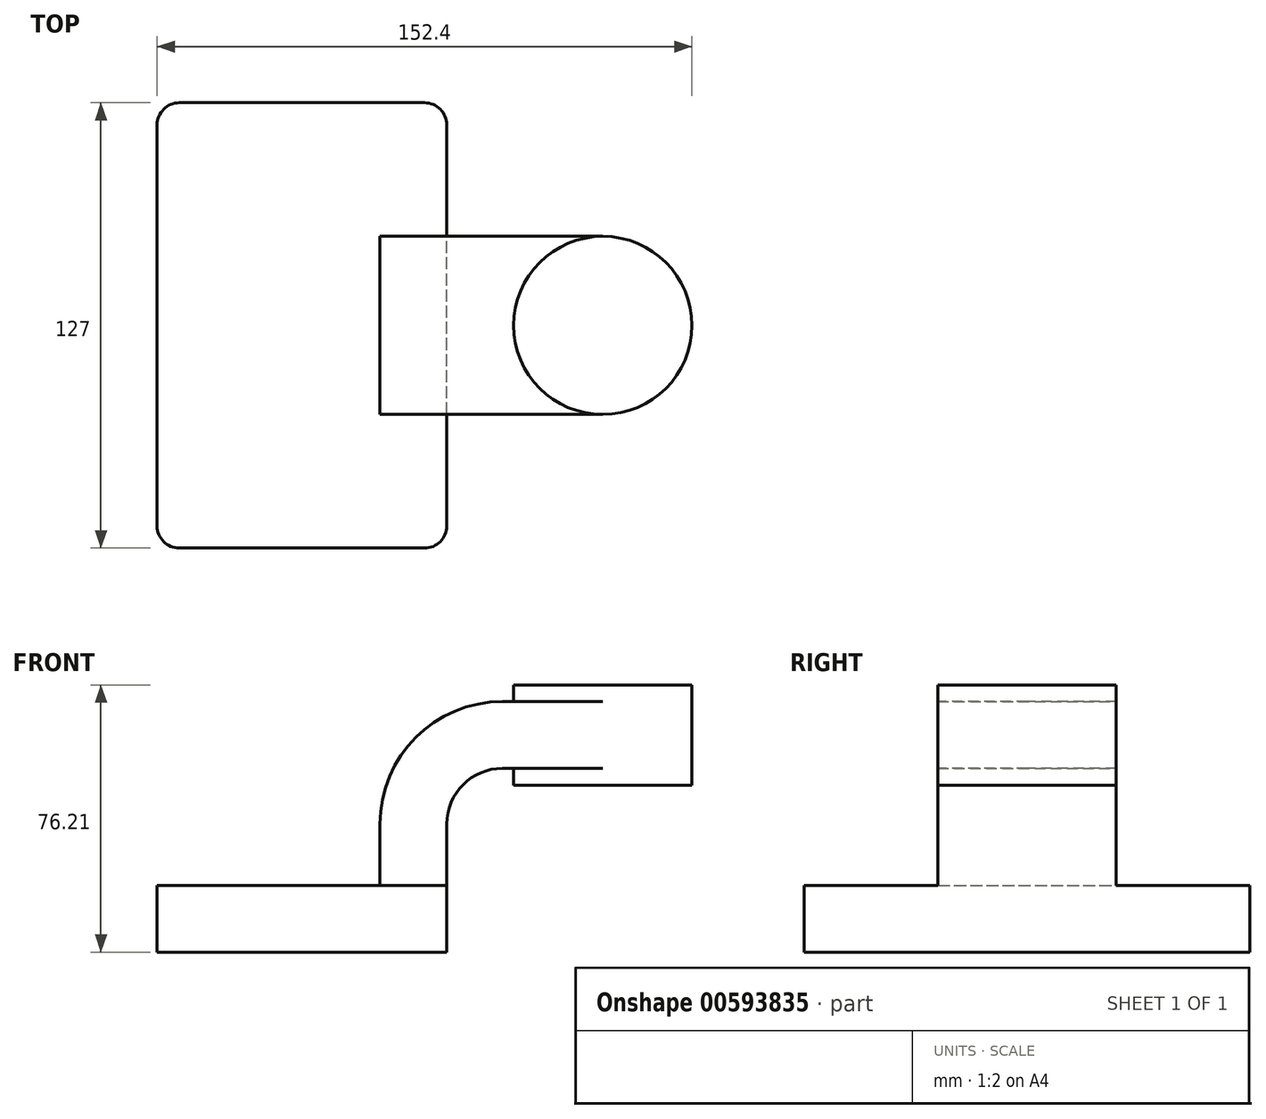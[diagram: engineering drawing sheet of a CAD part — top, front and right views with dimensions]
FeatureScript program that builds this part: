
annotation { "Feature Type Name" : "Feature", "Feature Type Description" : "" }
export const myFeature = defineFeature(function(context is Context, id is Id, definition is map)
    precondition{}
    {
        {
            var Q0;
            Q0=qCreatedBy(makeId("Front.planeOp"),FACE);
            var sketch = newSketch(context, id + "F0", { "sketchPlane" : qUnion([Q0])});
            skLineSegment(sketch, "E0.bottom", {"start": v(-41.28, -9.53) * mm, "end": v(41.28, -9.53) * mm});
            skLineSegment(sketch, "E0.top", {"start": v(-41.28, 9.53) * mm, "end": v(41.28, 9.53) * mm});
            skLineSegment(sketch, "E0.left", {"start": v(-41.28, -9.53) * mm, "end": v(-41.28, 9.53) * mm});
            skLineSegment(sketch, "E0.right", {"start": v(41.28, -9.53) * mm, "end": v(41.28, 9.53) * mm});
            skPoint(sketch, "E0.middle", {"position": v(0, 0) * mm});
            skLineSegment(sketch, "E1.bottom", {"start": v(60.33, 66.68) * mm, "end": v(111.12, 66.68) * mm});
            skLineSegment(sketch, "E1.top", {"start": v(60.33, 38.1) * mm, "end": v(111.12, 38.1) * mm});
            skLineSegment(sketch, "E1.left", {"start": v(60.33, 66.67) * mm, "end": v(60.33, 38.1) * mm});
            skLineSegment(sketch, "E1.right", {"start": v(111.13, 66.67) * mm, "end": v(111.13, 38.1) * mm});
            skPoint(sketch, "E1.middle", {"position": v(85.72, 52.39) * mm});
            skLineSegment(sketch, "E2", {"start": v(41.27, 9.53) * mm, "end": v(41.27, 27) * mm});
            skArc(sketch, "E3", {"start": v(41.27, 27) * mm, "mid": v(45.92, 38.23) * mm, "end": v(57.15, 42.88) * mm});
            skLineSegment(sketch, "E4", {"start": v(57.15, 42.88) * mm, "end": v(111.13, 42.88) * mm});
            skLineSegment(sketch, "E5.0", {"start": v(57.15, 61.93) * mm, "end": v(111.13, 61.93) * mm});
            skArc(sketch, "E5.1", {"start": v(22.22, 27) * mm, "mid": v(32.45, 51.7) * mm, "end": v(57.15, 61.93) * mm});
            skLineSegment(sketch, "E5.2", {"start": v(22.22, 9.53) * mm, "end": v(22.22, 27) * mm});
            skLineSegment(sketch, "E6", {"start": v(85.72, 38.1) * mm, "end": v(85.72, 66.67) * mm});
            skFitSpline(sketch, "E7", {"points": [v(-41.28, 9.53) * mm, v(57.15, 61.93) * mm], "startDerivative": vector(1.48, 78.93) * mm, "endDerivative": vector(142.25, -0.2) * mm});
            skSolve(sketch);
        }
        {
            var Q0;
            Q0=makeQuery(id+"F0.imprint","IMPRINT",FACE,{"disambiguationData":[TD([[makeQuery(id+"F0.imprint","IMPRINT",EDGE,{"derivedFrom":sQuery(id+"F0.wireOp",EDGE,"E0.bottom")}),1.0]])]});
            extrude(context, id + "F1", {"entities" : qUnion([Q0]), "endBound" : BoundingType.SYMMETRIC, "depth" : 127 * mm, "offsetDistance" : 25.4 * mm});
        }
        {
            var Q0;
            {var subQ1=sQuery(id+"F0.wireOp",EDGE,"E2");Q0=makeQuery(id+"F0.imprint","IMPRINT",FACE,{"disambiguationData":[TD([[makeQuery(id+"F0.imprint","IMPRINT",EDGE,{"derivedFrom":subQ1}),1.0]])]});}
            var Q1;
            {var subQ0=sQuery(id+"F0.wireOp",EDGE,"E5.0");var subQ1=sQuery(id+"F0.wireOp",EDGE,"E1.left");var subQ2=makeQuery(id+"F0.imprint","INTERSECT",VERTEX,{"derivedFrom":[subQ1,subQ0]});Q1=makeQuery(id+"F0.imprint","IMPRINT",FACE,{"disambiguationData":[TD([[makeQuery(id+"F0.imprint","IMPRINT",EDGE,{"disambiguationData":[TD([[subQ2,-1.0]])],"derivedFrom":subQ1}),1.0]])]});}
            extrude(context, id + "F2", {"entities" : qUnion([Q0, Q1]), "operationType" : NewBodyOperationType.ADD, "endBound" : BoundingType.SYMMETRIC, "depth" : 50.8 * mm, "offsetDistance" : 25.4 * mm});
        }
        {
            var Q0;
            Q0=makeQuery(id+"F0.imprint","IMPRINT",FACE,{"disambiguationData":[TD([[makeQuery(id+"F0.imprint","IMPRINT",EDGE,{"derivedFrom":sQuery(id+"F0.wireOp",EDGE,"E5.1")}),1.0]])]});
            extrude(context, id + "F3", {"entities" : qUnion([Q0]), "operationType" : NewBodyOperationType.ADD, "endBound" : BoundingType.SYMMETRIC, "depth" : 15.88 * mm, "offsetDistance" : 25.4 * mm});
        }
        {
            var Q0;
            {var subQ0=sQuery(id+"F0.wireOp",EDGE,"E1.right");Q0=makeQuery(id+"F0.imprint","IMPRINT",FACE,{"disambiguationData":[TD([[makeQuery(id+"F0.imprint","IMPRINT",EDGE,{"derivedFrom":subQ0}),-1.0]])]});}
            var Q1;
            Q1=sQuery(id+"F0.wireOp",EDGE,"E6");
            revolve(context, id + "F4", {"operationType" : NewBodyOperationType.ADD, "entities" : qUnion([Q0]), "axis" : qUnion([Q1]), "revolveType" : RevolveType.FULL});
        }
        {
            var Q0;
            Q0=makeQuery(id+"F1.opExtrude","CAP_EDGE",EDGE,{"disambiguationData":[OSD([sQuery(id+"F0.wireOp",EDGE,"E0.left")])],"isStart":false});
            var Q1;
            Q1=makeQuery(id+"F1.opExtrude","CAP_EDGE",EDGE,{"disambiguationData":[OSD([sQuery(id+"F0.wireOp",EDGE,"E0.right")])],"isStart":false});
            var Q2;
            Q2=makeQuery(id+"F1.opExtrude","CAP_EDGE",EDGE,{"disambiguationData":[OSD([sQuery(id+"F0.wireOp",EDGE,"E0.left")])],"isStart":true});
            var Q3;
            Q3=makeQuery(id+"F1.opExtrude","CAP_EDGE",EDGE,{"disambiguationData":[OSD([sQuery(id+"F0.wireOp",EDGE,"E0.right")])],"isStart":true});
            fillet(context, id + "F5", {"entities" : qUnion([Q0, Q1, Q2, Q3]), "radius" : 6.35 * mm, "tangentPropagation" : true, "allowEdgeOverflow" : false});
        }
    });
